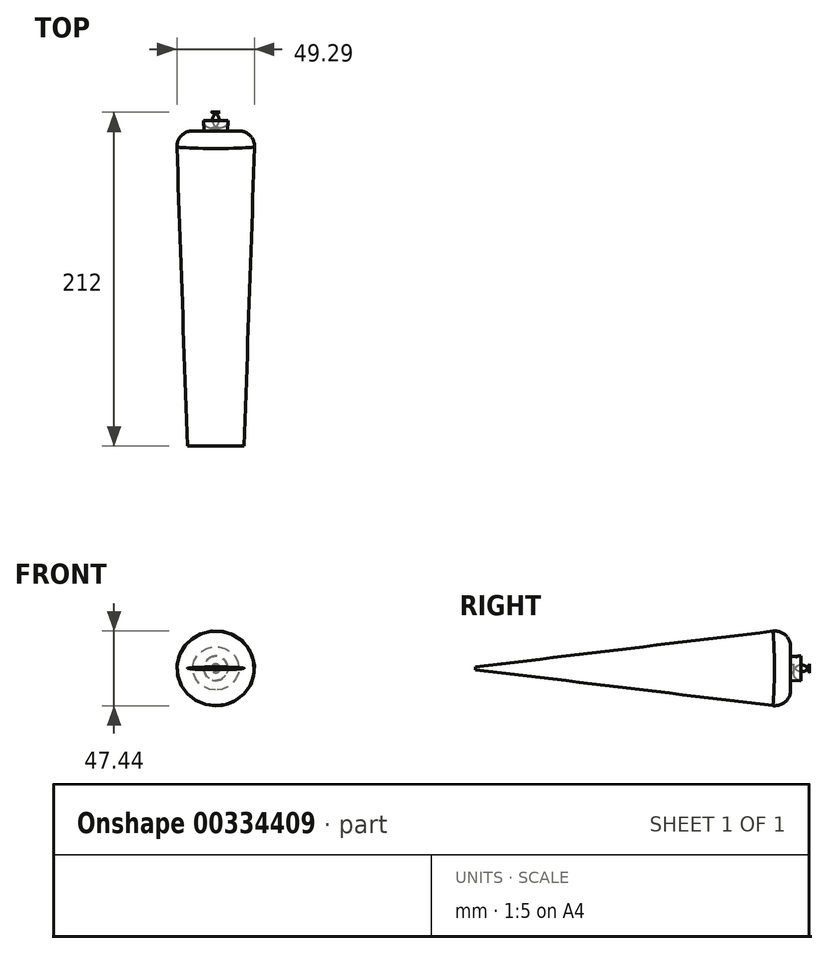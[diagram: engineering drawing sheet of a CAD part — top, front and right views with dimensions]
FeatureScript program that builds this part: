
annotation { "Feature Type Name" : "Feature", "Feature Type Description" : "" }
export const myFeature = defineFeature(function(context is Context, id is Id, definition is map)
    precondition{}
    {
        {
            var Q0;
            Q0=qCreatedBy(makeId("Front.planeOp"),FACE);
            var sketch = newSketch(context, id + "F0", { "sketchPlane" : qUnion([Q0])});
            skCircle(sketch, "E0", {"center": v(0, 0) * mm, "radius": 25 * mm});
            skSolve(sketch);
        }
        {
            var Q0;
            Q0=makeQuery(id+"F0.imprint","IMPRINT",FACE,{"disambiguationData":[TD([[makeQuery(id+"F0.imprint","IMPRINT",EDGE,{"derivedFrom":sQuery(id+"F0.wireOp",EDGE,"E0")}),1.0]])]});
            cPlane(context, id + "F1", {"entities" : qUnion([Q0]), "cplaneType" : CPlaneType.OFFSET, "offset" : 200.2 * mm, "width" : 150 * mm, "height" : 150 * mm});
        }
        {
            var Q0;
            Q0=qCreatedBy(id+"F1.planeOp",FACE);
            var sketch = newSketch(context, id + "F2", { "sketchPlane" : qUnion([Q0])});
            skEllipse(sketch, "E1", {"center": v(0, 0) * mm, "majorRadius": 18.02 * mm, "minorRadius": 0.85 * mm, "majorAxis": v(1, 0)});
            skSolve(sketch);
        }
        {
            var Q0;
            Q0=makeQuery(id+"F0.imprint","IMPRINT",FACE,{"disambiguationData":[TD([[makeQuery(id+"F0.imprint","IMPRINT",EDGE,{"derivedFrom":sQuery(id+"F0.wireOp",EDGE,"E0")}),1.0]])]});
            var Q1;
            Q1=makeQuery(id+"F2.imprint","IMPRINT",FACE,{"disambiguationData":[TD([[makeQuery(id+"F2.imprint","IMPRINT",EDGE,{"derivedFrom":sQuery(id+"F2.wireOp",EDGE,"E1")}),1.0]])]});
            loft(context, id + "F3", {"sheetProfilesArray" : [{ "sheetProfileEntities" : qUnion([Q0]) }, { "sheetProfileEntities" : qUnion([Q1]) }]});
        }
        {
            var Q0;
            Q0=makeQuery(id+"F3.opLoft","MID_CAP_EDGE",EDGE,{"disambiguationData":[OSD([sQuery(id+"F0.wireOp",EDGE,"E0")])],"capPos":0.0});
            fillet(context, id + "F4", {"entities" : qUnion([Q0]), "radius" : 10 * mm, "tangentPropagation" : true, "allowEdgeOverflow" : false});
        }
        {
            var Q0;
            Q0=makeQuery(id+"F3.opLoft","CAP_FACE",FACE,{"disambiguationData":[OSD([makeQuery(id+"F0.imprint","IMPRINT",FACE,{"disambiguationData":[TD([[makeQuery(id+"F0.imprint","IMPRINT",EDGE,{"derivedFrom":sQuery(id+"F0.wireOp",EDGE,"E0")}),1.0]])]})])],"isStart":true});
            var sketch = newSketch(context, id + "F5", { "sketchPlane" : qUnion([Q0])});
            skCircle(sketch, "E2", {"center": v(0, 0) * mm, "radius": 7.5 * mm});
            skSolve(sketch);
        }
        {
            var Q0;
            Q0 = qSketchRegion(id + "F5", true);
            extrude(context, id + "F6", {"entities" : qUnion([Q0]), "operationType" : NewBodyOperationType.ADD, "depth" : 11.8 * mm, "hasDraft" : true, "draftAngle" : 3 * degree});
        }
        {
            var Q0;
            Q0=makeQuery(id+"F6.opExtrude","CAP_EDGE",EDGE,{"disambiguationData":[OSD([sQuery(id+"F5.wireOp",EDGE,"E2")])],"isStart":false});
            fillet(context, id + "F7", {"entities" : qUnion([Q0]), "radius" : 5 * mm, "tangentPropagation" : true, "allowEdgeOverflow" : false});
        }
    });
